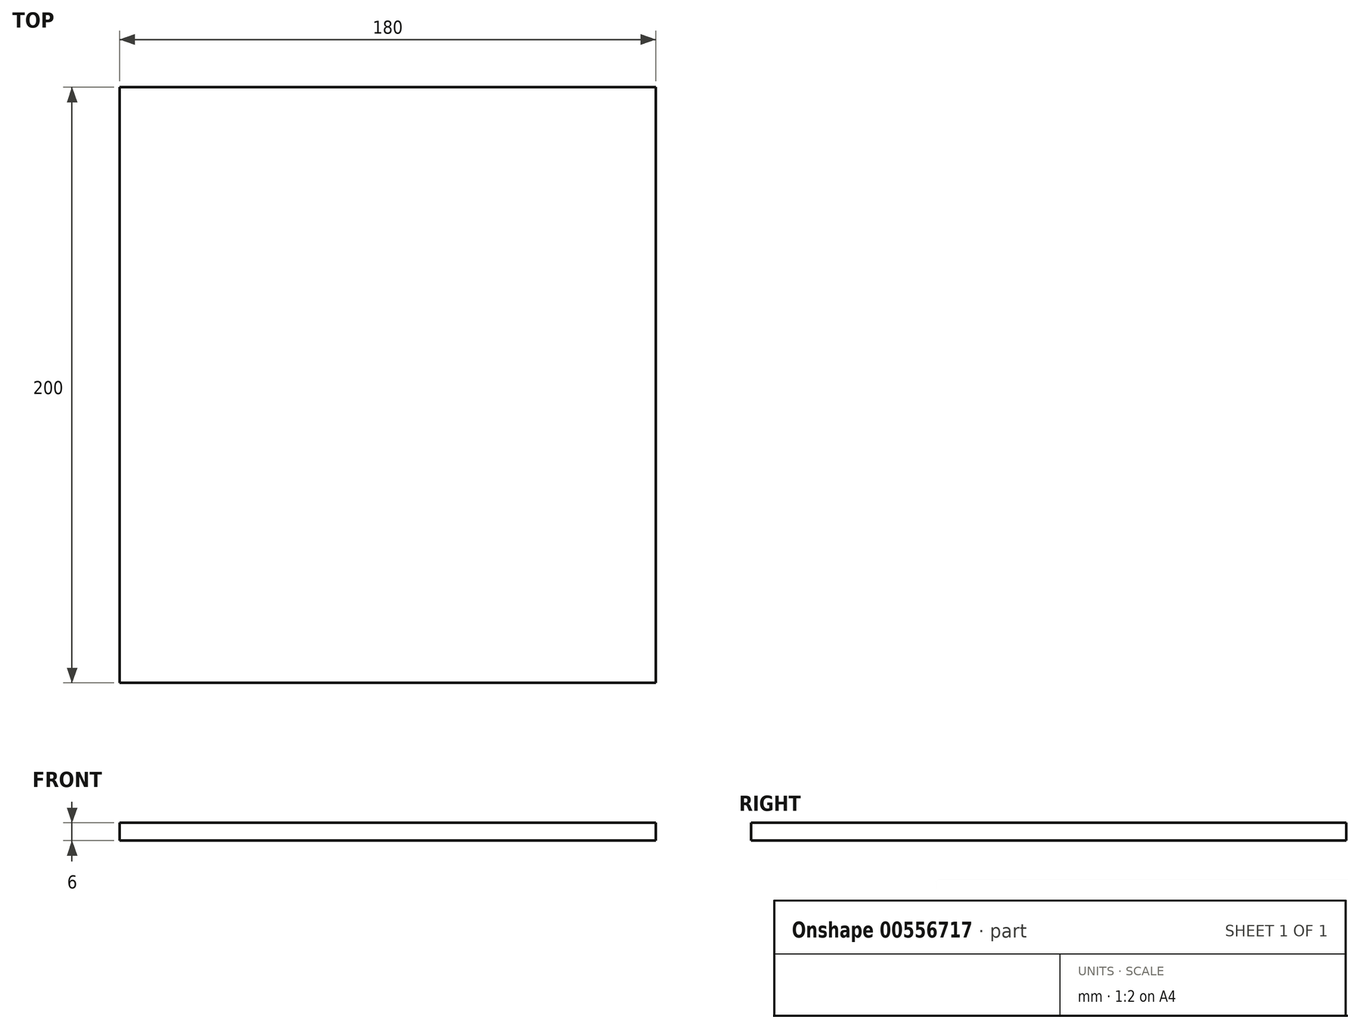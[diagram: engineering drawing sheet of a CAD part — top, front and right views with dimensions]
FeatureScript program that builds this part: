
annotation { "Feature Type Name" : "Feature", "Feature Type Description" : "" }
export const myFeature = defineFeature(function(context is Context, id is Id, definition is map)
    precondition{}
    {
        {
            var Q0;
            Q0=qCreatedBy(makeId("Top.planeOp"),FACE);
            var sketch = newSketch(context, id + "F0", { "sketchPlane" : qUnion([Q0])});
            skLineSegment(sketch, "E0", {"start": v(0, 0) * mm, "end": v(0, -200) * mm});
            skLineSegment(sketch, "E1", {"start": v(0, -200) * mm, "end": v(180, -200) * mm});
            skLineSegment(sketch, "E2", {"start": v(180, -200) * mm, "end": v(180, 0) * mm});
            skLineSegment(sketch, "E3", {"start": v(180, 0) * mm, "end": v(0, 0) * mm});
            skSolve(sketch);
        }
        {
            var Q0;
            Q0=makeQuery(id+"F0.imprint","IMPRINT",FACE,{"disambiguationData":[TD([[makeQuery(id+"F0.imprint","IMPRINT",EDGE,{"derivedFrom":sQuery(id+"F0.wireOp",EDGE,"E0")}),1.0]])]});
            extrude(context, id + "F1", {"entities" : qUnion([Q0]), "depth" : 6 * mm, "offsetDistance" : 25 * mm, "symmetric" : true});
        }
    });
